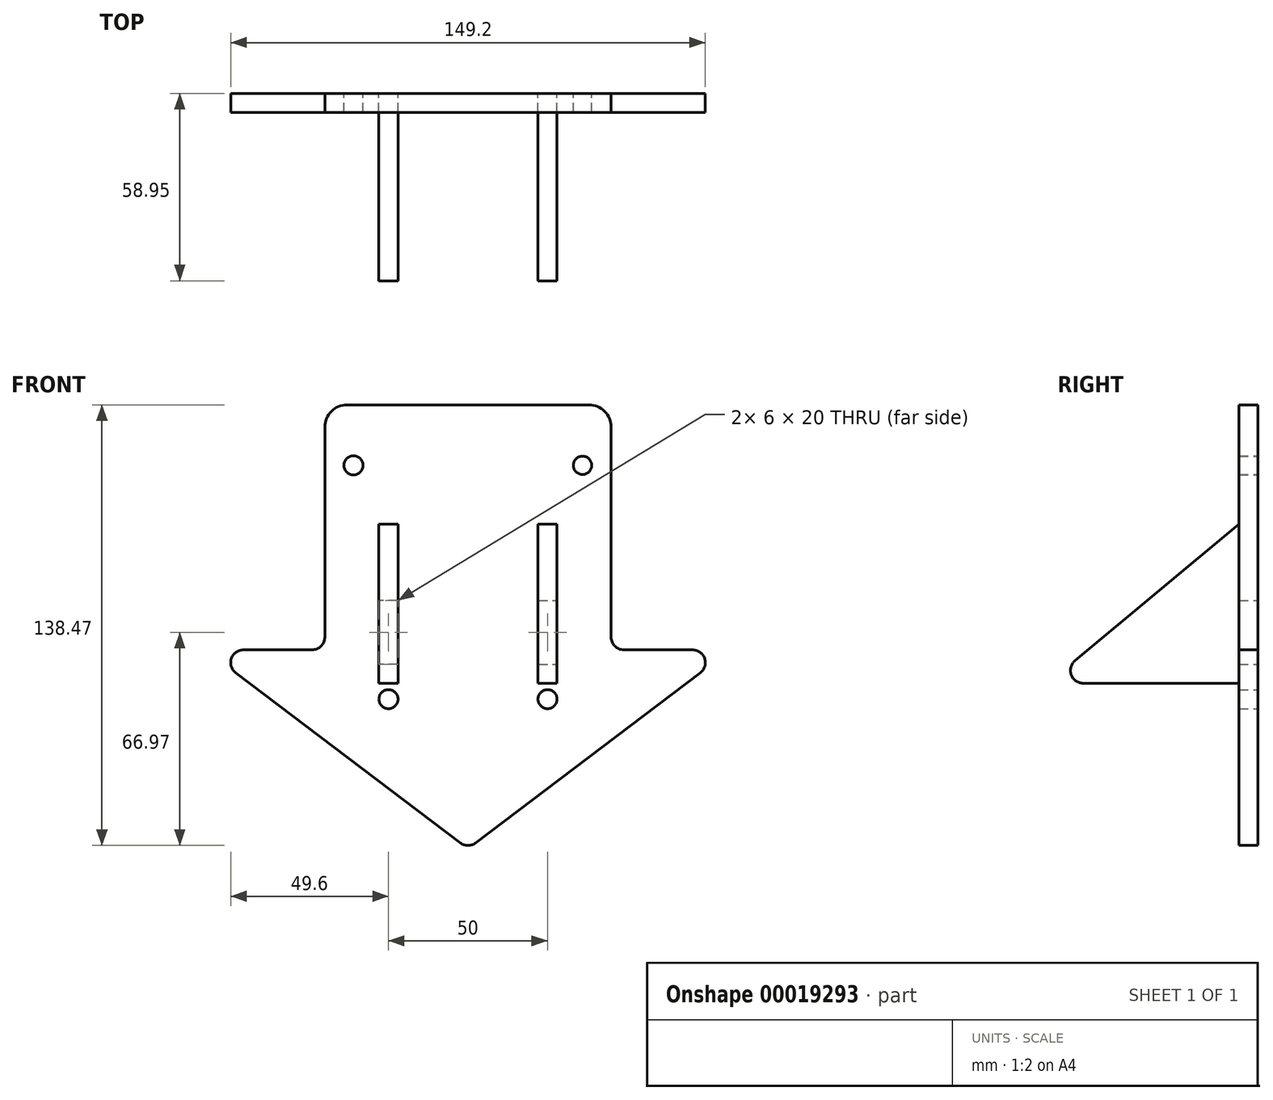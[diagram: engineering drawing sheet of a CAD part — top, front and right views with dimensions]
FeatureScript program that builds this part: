
annotation { "Feature Type Name" : "Feature", "Feature Type Description" : "" }
export const myFeature = defineFeature(function(context is Context, id is Id, definition is map)
    precondition{}
    {
        {
            var Q0;
            Q0=qCreatedBy(makeId("Front.planeOp"),FACE);
            var sketch = newSketch(context, id + "F0", { "sketchPlane" : qUnion([Q0])});
            skLineSegment(sketch, "E0", {"start": v(-36, -19) * mm, "end": v(36, -19) * mm, "construction": true});
            skLineSegment(sketch, "E1", {"start": v(0, 35) * mm, "end": v(0, -37) * mm, "construction": true});
            skLineSegment(sketch, "E2", {"start": v(0, -37) * mm, "end": v(0, -92.5) * mm, "construction": true});
            skLineSegment(sketch, "E3", {"start": v(-25, -92.5) * mm, "end": v(25, -92.5) * mm, "construction": true});
            skLineSegment(sketch, "E4", {"start": v(-31.74, 0) * mm, "end": v(31.74, 0) * mm});
            skLineSegment(sketch, "E5", {"start": v(31.74, 0) * mm, "end": v(31.74, 0) * mm});
            skCircle(sketch, "E6", {"center": v(-36, -19) * mm, "radius": 3 * mm});
            skCircle(sketch, "E7", {"center": v(36, -19) * mm, "radius": 2.9 * mm});
            skLineSegment(sketch, "E8", {"start": v(-31.74, 0) * mm, "end": v(-38, 0) * mm});
            skLineSegment(sketch, "E9", {"start": v(31.74, 0) * mm, "end": v(38, 0) * mm});
            skArc(sketch, "E10", {"start": v(-38, 0) * mm, "mid": v(-42.95, -2.05) * mm, "end": v(-45, -7) * mm});
            skArc(sketch, "E11", {"start": v(45, -7) * mm, "mid": v(42.95, -2.05) * mm, "end": v(38, 0) * mm});
            skCircle(sketch, "E12", {"center": v(-25, -92.5) * mm, "radius": 3 * mm});
            skCircle(sketch, "E13", {"center": v(25, -92.5) * mm, "radius": 3 * mm});
            skLineSegment(sketch, "E14", {"start": v(-36, -19) * mm, "end": v(-36, -22) * mm, "construction": true});
            skLineSegment(sketch, "E15", {"start": v(36, -19) * mm, "end": v(36, -22) * mm, "construction": true});
            skLineSegment(sketch, "E16", {"start": v(-45, -7) * mm, "end": v(-45, -77) * mm});
            skLineSegment(sketch, "E17", {"start": v(45, -7) * mm, "end": v(45, -77) * mm});
            skLineSegment(sketch, "E18.bottom", {"start": v(-28, -61.5) * mm, "end": v(-22, -61.5) * mm});
            skLineSegment(sketch, "E18.top", {"start": v(-28, -81.5) * mm, "end": v(-22, -81.5) * mm});
            skLineSegment(sketch, "E18.left", {"start": v(-28, -61.5) * mm, "end": v(-28, -81.5) * mm});
            skLineSegment(sketch, "E18.right", {"start": v(-22, -61.5) * mm, "end": v(-22, -81.5) * mm});
            skLineSegment(sketch, "E19.bottom", {"start": v(22, -61.5) * mm, "end": v(28, -61.5) * mm});
            skLineSegment(sketch, "E19.top", {"start": v(22, -81.5) * mm, "end": v(28, -81.5) * mm});
            skLineSegment(sketch, "E19.left", {"start": v(22, -61.5) * mm, "end": v(22, -81.5) * mm});
            skLineSegment(sketch, "E19.right", {"start": v(28, -61.5) * mm, "end": v(28, -81.5) * mm});
            skLineSegment(sketch, "E20", {"start": v(-25, -61.5) * mm, "end": v(-25, -81.5) * mm, "construction": true});
            skLineSegment(sketch, "E21", {"start": v(25, -61.5) * mm, "end": v(25, -81.5) * mm, "construction": true});
            skPoint(sketch, "E22", {"position": v(0, -19) * mm});
            skLineSegment(sketch, "E23", {"start": v(82.5, -77) * mm, "end": v(0, -139.5) * mm});
            skLineSegment(sketch, "E24", {"start": v(0, -139.5) * mm, "end": v(-82.5, -77) * mm});
            skLineSegment(sketch, "E25", {"start": v(-82.5, -77) * mm, "end": v(-45, -77) * mm});
            skLineSegment(sketch, "E26", {"start": v(82.5, -77) * mm, "end": v(45, -77) * mm});
            skSolve(sketch);
        }
        {
            var Q0;
            Q0=qSketchRegion(id+"F0",true);
            extrude(context, id + "F1", {"entities" : qUnion([Q0]), "depth" : 6 * mm});
        }
        {
            var Q0;
            Q0=makeQuery(id+"F1.opExtrude","SWEPT_FACE",FACE,{"disambiguationData":[OSD([sQuery(id+"F0.wireOp",EDGE,"E18.left")])]});
            var sketch = newSketch(context, id + "F2", { "sketchPlane" : qUnion([Q0])});
            skLineSegment(sketch, "E27", {"start": v(0, -81.5) * mm, "end": v(-6, -81.5) * mm});
            skLineSegment(sketch, "E28", {"start": v(-6, -81.5) * mm, "end": v(-6, -87.5) * mm});
            skLineSegment(sketch, "E29", {"start": v(-6, -87.5) * mm, "end": v(-66, -87.5) * mm});
            skLineSegment(sketch, "E30", {"start": v(-66, -87.5) * mm, "end": v(-6, -37.5) * mm});
            skLineSegment(sketch, "E31", {"start": v(-6, -37.5) * mm, "end": v(-6, -61.5) * mm});
            skLineSegment(sketch, "E32", {"start": v(-6, -61.5) * mm, "end": v(0, -61.5) * mm});
            skLineSegment(sketch, "E33", {"start": v(0, -61.5) * mm, "end": v(0, -81.5) * mm});
            skSolve(sketch);
        }
        {
            var Q0;
            Q0=qSketchRegion(id+"F2",true);
            extrude(context, id + "F3", {"entities" : qUnion([Q0]), "depth" : 6 * mm});
        }
        {
            var Q0;
            Q0=makeQuery(id+"F3.opExtrude","SWEPT_BODY",BODY,{"disambiguationData":[OSD([sQuery(id+"F2.wireOp",EDGE,"E27"),sQuery(id+"F2.wireOp",EDGE,"E28"),sQuery(id+"F2.wireOp",EDGE,"E29"),sQuery(id+"F2.wireOp",EDGE,"E30"),sQuery(id+"F2.wireOp",EDGE,"E31"),sQuery(id+"F2.wireOp",EDGE,"E32"),sQuery(id+"F2.wireOp",EDGE,"E33")])]});
            var Q1;
            Q1=qCreatedBy(makeId("Right.planeOp"),FACE);
            mirror(context, id + "F4", {"entities" : qUnion([Q0]), "mirrorPlane" : qUnion([Q1])});
        }
        {
            var Q0;
            Q0=makeQuery(id+"F1.opExtrude","SWEPT_EDGE",EDGE,{"disambiguationData":[OSD([sQuery(id+"F0.wireOp",EDGE,"E23"),sQuery(id+"F0.wireOp",EDGE,"E26")])]});
            var Q1;
            Q1=makeQuery(id+"F1.opExtrude","SWEPT_EDGE",EDGE,{"disambiguationData":[OSD([sQuery(id+"F0.wireOp",EDGE,"E24"),sQuery(id+"F0.wireOp",EDGE,"E25")])]});
            var Q2;
            Q2=makeQuery(id+"F1.opExtrude","SWEPT_EDGE",EDGE,{"disambiguationData":[OSD([sQuery(id+"F0.wireOp",EDGE,"E23"),sQuery(id+"F0.wireOp",EDGE,"E24")])]});
            var Q3;
            Q3=makeQuery(id+"F1.opExtrude","SWEPT_EDGE",EDGE,{"disambiguationData":[OSD([sQuery(id+"F0.wireOp",EDGE,"E17"),sQuery(id+"F0.wireOp",EDGE,"E26")])]});
            var Q4;
            Q4=makeQuery(id+"F1.opExtrude","SWEPT_EDGE",EDGE,{"disambiguationData":[OSD([sQuery(id+"F0.wireOp",EDGE,"E16"),sQuery(id+"F0.wireOp",EDGE,"E25")])]});
            var Q5;
            Q5=makeQuery(id+"F3.opExtrude","SWEPT_EDGE",EDGE,{"disambiguationData":[OSD([sQuery(id+"F2.wireOp",EDGE,"E29"),sQuery(id+"F2.wireOp",EDGE,"E30")])]});
            var Q6;
            Q6=makeQuery(id+"F4.opPattern","COPY",EDGE,{"derivedFrom":makeQuery(id+"F3.opExtrude","SWEPT_EDGE",EDGE,{"disambiguationData":[OSD([sQuery(id+"F2.wireOp",EDGE,"E29"),sQuery(id+"F2.wireOp",EDGE,"E30")])]}),"instanceName":"1"});
            fillet(context, id + "F5", {"entities" : qUnion([Q0, Q1, Q2, Q3, Q4, Q5, Q6]), "radius" : 4 * mm, "tangentPropagation" : true, "allowEdgeOverflow" : false});
        }
    });
